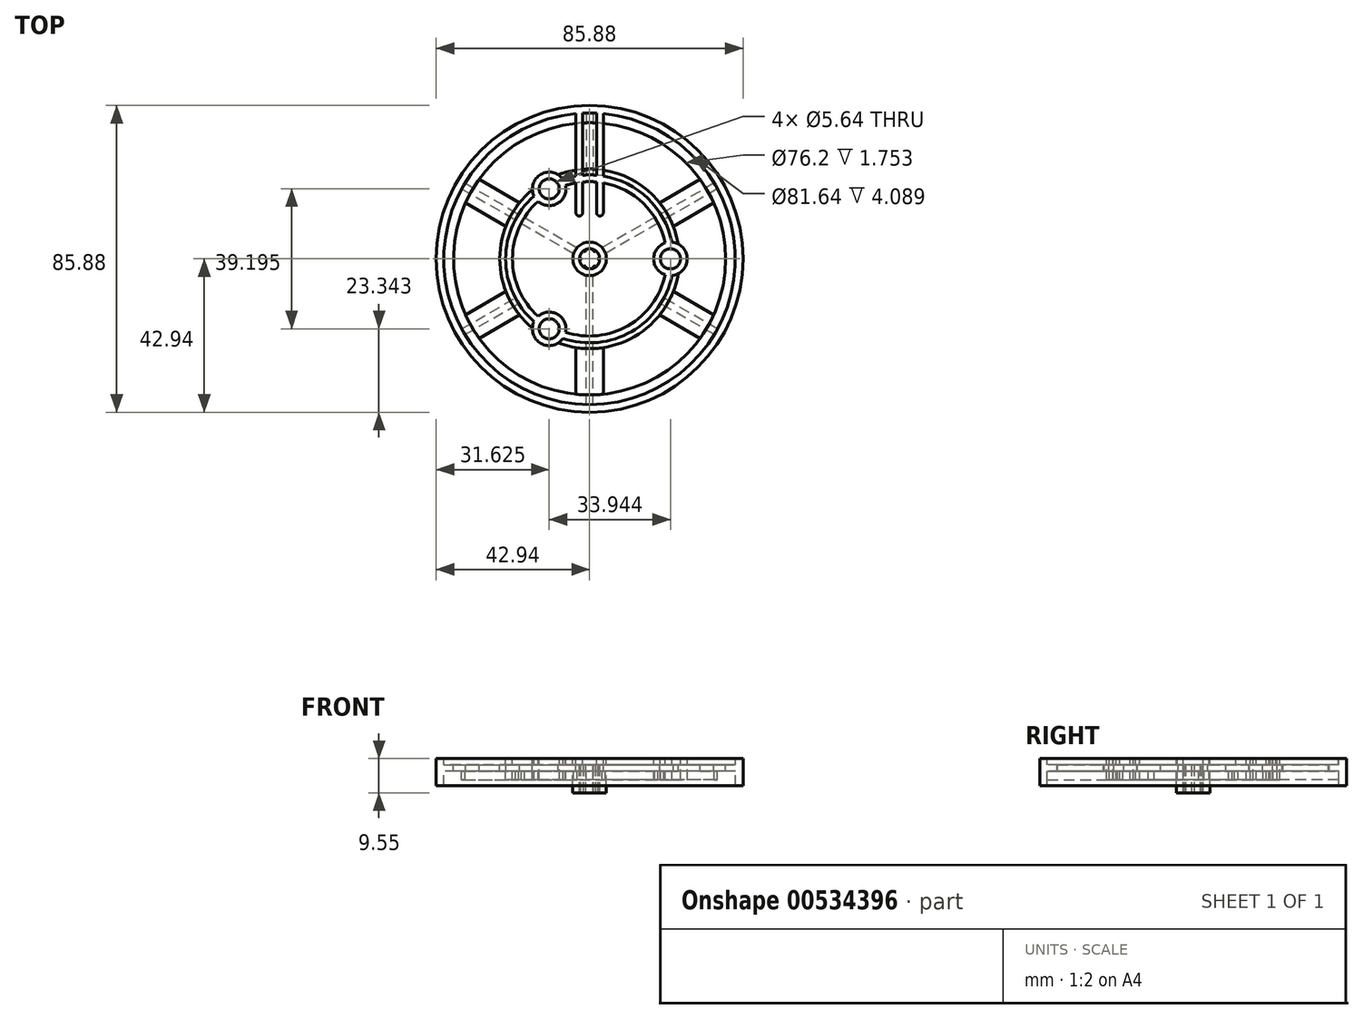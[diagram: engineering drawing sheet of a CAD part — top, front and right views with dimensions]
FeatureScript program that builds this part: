
annotation { "Feature Type Name" : "Feature", "Feature Type Description" : "" }
export const myFeature = defineFeature(function(context is Context, id is Id, definition is map)
    precondition{}
    {
        {
            var Q0;
            Q0=qCreatedBy(makeId("Front.planeOp"),FACE);
            var sketch = newSketch(context, id + "F0", { "sketchPlane" : qUnion([Q0])});
            skLineSegment(sketch, "E0", {"start": v(2.82, 0) * mm, "end": v(2.82, -9.55) * mm});
            skLineSegment(sketch, "E1", {"start": v(2.82, 0) * mm, "end": v(4.7, 0) * mm});
            skLineSegment(sketch, "E2", {"start": v(4.7, 0) * mm, "end": v(4.7, -1.75) * mm});
            skLineSegment(sketch, "E3", {"start": v(4.7, -1.75) * mm, "end": v(21.6, -1.75) * mm});
            skLineSegment(sketch, "E4", {"start": v(21.6, -1.75) * mm, "end": v(21.6, 0) * mm});
            skLineSegment(sketch, "E5", {"start": v(21.6, 0) * mm, "end": v(23.5, 0) * mm});
            skLineSegment(sketch, "E6", {"start": v(23.5, 0) * mm, "end": v(23.5, -1.75) * mm});
            skLineSegment(sketch, "E7", {"start": v(23.5, -1.75) * mm, "end": v(25.15, -1.75) * mm});
            skLineSegment(sketch, "E8", {"start": v(25.15, -1.75) * mm, "end": v(25.15, -3.5) * mm});
            skLineSegment(sketch, "E9", {"start": v(25.15, -3.5) * mm, "end": v(23.5, -3.5) * mm});
            skLineSegment(sketch, "E10", {"start": v(23.5, -3.5) * mm, "end": v(23.5, -5.94) * mm});
            skLineSegment(sketch, "E11", {"start": v(23.5, -5.94) * mm, "end": v(21.6, -5.94) * mm});
            skLineSegment(sketch, "E12", {"start": v(21.6, -5.94) * mm, "end": v(21.6, -3.5) * mm});
            skLineSegment(sketch, "E13", {"start": v(21.6, -3.5) * mm, "end": v(4.7, -3.5) * mm});
            skLineSegment(sketch, "E14", {"start": v(4.7, -3.5) * mm, "end": v(4.7, -9.55) * mm});
            skLineSegment(sketch, "E15", {"start": v(4.7, -9.55) * mm, "end": v(2.82, -9.55) * mm});
            skLineSegment(sketch, "E16", {"start": v(38.1, -1.75) * mm, "end": v(38.1, -3.5) * mm});
            skLineSegment(sketch, "E17", {"start": v(38.1, -3.5) * mm, "end": v(40.82, -3.5) * mm});
            skLineSegment(sketch, "E18", {"start": v(40.82, -3.5) * mm, "end": v(40.82, -7.6) * mm});
            skLineSegment(sketch, "E19", {"start": v(40.82, -7.6) * mm, "end": v(42.94, -7.6) * mm});
            skLineSegment(sketch, "E20", {"start": v(42.94, -7.6) * mm, "end": v(42.94, 0) * mm});
            skLineSegment(sketch, "E21", {"start": v(42.94, 0) * mm, "end": v(40.82, 0) * mm});
            skLineSegment(sketch, "E22", {"start": v(40.82, 0) * mm, "end": v(40.82, -1.75) * mm});
            skLineSegment(sketch, "E23", {"start": v(40.82, -1.75) * mm, "end": v(38.1, -1.75) * mm});
            skLineSegment(sketch, "E24", {"start": v(0, 0) * mm, "end": v(0, -9.55) * mm});
            skSolve(sketch);
        }
        {
            var Q0;
            Q0=qSketchRegion(id+"F0",true);
            var Q1;
            Q1=sQuery(id+"F0.wireOp",EDGE,"E24");
            revolve(context, id + "F1", {"entities" : qUnion([Q0]), "axis" : qUnion([Q1]), "revolveType" : RevolveType.FULL});
        }
        {
            var Q0;
            Q0=makeQuery(id+"F1.opRevolve","SWEPT_FACE",FACE,{"disambiguationData":[OSD([sQuery(id+"F0.wireOp",EDGE,"E21")])]});
            var sketch = newSketch(context, id + "F2", { "sketchPlane" : qUnion([Q0])});
            skCircle(sketch, "E25", {"center": v(0, 0) * mm, "radius": 13.46 * mm, "construction": true});
            skLineSegment(sketch, "E26", {"start": v(-3.82, 40.64) * mm, "end": v(-3.82, 12.9) * mm});
            skLineSegment(sketch, "E27", {"start": v(3.82, 40.64) * mm, "end": v(3.82, 12.9) * mm});
            skLineSegment(sketch, "E28", {"start": v(-1.97, 40.77) * mm, "end": v(-1.97, 12.9) * mm});
            skLineSegment(sketch, "E29", {"start": v(1.97, 40.77) * mm, "end": v(1.97, 12.9) * mm});
            skArc(sketch, "E30", {"start": v(-3.82, 12.9) * mm, "mid": v(-2.9, 11.98) * mm, "end": v(-1.97, 12.9) * mm});
            skArc(sketch, "E31", {"start": v(1.97, 12.9) * mm, "mid": v(2.9, 11.98) * mm, "end": v(3.82, 12.9) * mm});
            skArc(sketch, "E32", {"start": v(-1.97, 40.77) * mm, "mid": v(-2.9, 40.71) * mm, "end": v(-3.82, 40.64) * mm});
            skArc(sketch, "E33", {"start": v(1.97, 40.77) * mm, "mid": v(2.9, 40.71) * mm, "end": v(3.82, 40.64) * mm});
            skSolve(sketch);
        }
        {
            var Q0;
            Q0=makeQuery(id+"F2.imprint","IMPRINT",FACE,{"disambiguationData":[TD([[makeQuery(id+"F2.imprint","IMPRINT",EDGE,{"derivedFrom":sQuery(id+"F2.wireOp",EDGE,"E26")}),1.0]])]});
            var Q1;
            Q1=qSketchRegion(id+"F2",true);
            var Q2;
            Q2=makeQuery(id+"F1.opRevolve","SWEPT_FACE",FACE,{"disambiguationData":[OSD([sQuery(id+"F0.wireOp",EDGE,"E23")])]});
            extrude(context, id + "F3", {"entities" : qUnion([Q0, Q1]), "operationType" : NewBodyOperationType.ADD, "endBound" : BoundingType.UP_TO_SURFACE, "oppositeDirection" : true, "depth" : 25.4 * mm, "endBoundEntityFace" : qUnion([Q2]), "offsetDistance" : 25.4 * mm});
        }
        {
            var Q0;
            Q0=makeQuery(id+"F3.opExtrude","CAP_FACE",FACE,{"disambiguationData":[OSD([sQuery(id+"F2.wireOp",EDGE,"E27"),sQuery(id+"F2.wireOp",EDGE,"E29"),sQuery(id+"F2.wireOp",EDGE,"E31"),sQuery(id+"F2.wireOp",EDGE,"E33")])],"isStart":false});
            var sketch = newSketch(context, id + "F4", { "sketchPlane" : qUnion([Q0])});
            skArc(sketch, "E34.0", {"start": v(-3.82, -24.85) * mm, "mid": v(0, -25.15) * mm, "end": v(3.82, -24.85) * mm});
            skArc(sketch, "E35.0", {"start": v(-3.82, -37.9) * mm, "mid": v(0, -38.1) * mm, "end": v(3.82, -37.9) * mm});
            skLineSegment(sketch, "E36.0", {"start": v(-3.82, -37.9) * mm, "end": v(-3.82, -24.85) * mm});
            skLineSegment(sketch, "E37.0", {"start": v(3.82, -37.9) * mm, "end": v(3.82, -24.85) * mm});
            skPoint(sketch, "E38.orphan", {"position": v(-3.82, -12.9) * mm});
            skPoint(sketch, "E39.orphan", {"position": v(-3.82, -21.26) * mm});
            skSolve(sketch);
        }
        {
            var Q0;
            Q0=qSketchRegion(id+"F4",true);
            var Q1;
            Q1=makeQuery(id+"F1.opRevolve","SWEPT_FACE",FACE,{"disambiguationData":[OSD([sQuery(id+"F0.wireOp",EDGE,"E9")])]});
            extrude(context, id + "F5", {"entities" : qUnion([Q0]), "endBound" : BoundingType.UP_TO_SURFACE, "depth" : 25.4 * mm, "endBoundEntityFace" : qUnion([Q1]), "offsetDistance" : 25.4 * mm});
        }
        {
            var Q0;
            Q0=makeQuery(id+"F5.opExtrude","CAP_FACE",FACE,{"disambiguationData":[OSD([sQuery(id+"F4.wireOp",EDGE,"E34.0"),sQuery(id+"F4.wireOp",EDGE,"E35.0"),sQuery(id+"F4.wireOp",EDGE,"E36.0"),sQuery(id+"F4.wireOp",EDGE,"E37.0")])],"isStart":false});
            var sketch = newSketch(context, id + "F6", { "sketchPlane" : qUnion([Q0])});
            skLineSegment(sketch, "E40", {"start": v(-0.93, -25.13) * mm, "end": v(-0.93, -38.09) * mm});
            skLineSegment(sketch, "E41", {"start": v(0.93, -25.13) * mm, "end": v(0.93, -38.09) * mm});
            skArc(sketch, "E42.0", {"start": v(-0.93, -23.49) * mm, "mid": v(0, -23.5) * mm, "end": v(0.93, -23.49) * mm});
            skArc(sketch, "E43.0", {"start": v(-0.93, -40.8) * mm, "mid": v(0, -40.82) * mm, "end": v(0.93, -40.8) * mm});
            skLineSegment(sketch, "E44", {"start": v(-0.93, -25.13) * mm, "end": v(-0.93, -23.49) * mm});
            skLineSegment(sketch, "E45", {"start": v(0.93, -25.13) * mm, "end": v(0.93, -23.49) * mm});
            skLineSegment(sketch, "E46", {"start": v(-0.93, -38.09) * mm, "end": v(-0.93, -40.8) * mm});
            skLineSegment(sketch, "E47", {"start": v(0.93, -38.09) * mm, "end": v(0.93, -40.8) * mm});
            skLineSegment(sketch, "E48", {"start": v(0, -27.2) * mm, "end": v(0, -23.5) * mm, "construction": true});
            skSolve(sketch);
        }
        {
            var Q0;
            Q0=qSketchRegion(id+"F6",true);
            var Q1;
            Q1=makeQuery(id+"F1.opRevolve","SWEPT_FACE",FACE,{"disambiguationData":[OSD([sQuery(id+"F0.wireOp",EDGE,"E11")])]});
            extrude(context, id + "F7", {"entities" : qUnion([Q0]), "endBound" : BoundingType.UP_TO_SURFACE, "depth" : 25.4 * mm, "endBoundEntityFace" : qUnion([Q1]), "offsetDistance" : 25.4 * mm});
        }
        {
            var Q0;
            Q0=makeQuery(id+"F3.opExtrude","SWEPT_BODY",BODY,{"disambiguationData":[OSD([sQuery(id+"F2.wireOp",EDGE,"E26"),sQuery(id+"F2.wireOp",EDGE,"E28"),sQuery(id+"F2.wireOp",EDGE,"E30"),sQuery(id+"F2.wireOp",EDGE,"E32")])]});
            var Q1;
            Q1=makeQuery(id+"F3.opExtrude","SWEPT_BODY",BODY,{"disambiguationData":[OSD([sQuery(id+"F2.wireOp",EDGE,"E27"),sQuery(id+"F2.wireOp",EDGE,"E29"),sQuery(id+"F2.wireOp",EDGE,"E31"),sQuery(id+"F2.wireOp",EDGE,"E33")])]});
            var Q2;
            Q2=makeQuery(id+"F5.opExtrude","SWEPT_BODY",BODY,{"disambiguationData":[OSD([sQuery(id+"F4.wireOp",EDGE,"E34.0"),sQuery(id+"F4.wireOp",EDGE,"E35.0"),sQuery(id+"F4.wireOp",EDGE,"E36.0"),sQuery(id+"F4.wireOp",EDGE,"E37.0")])]});
            var Q3;
            Q3=makeQuery(id+"F7.opExtrude","SWEPT_BODY",BODY,{"disambiguationData":[OSD([sQuery(id+"F6.wireOp",EDGE,"E40"),sQuery(id+"F6.wireOp",EDGE,"E41"),sQuery(id+"F6.wireOp",EDGE,"E42.0"),sQuery(id+"F6.wireOp",EDGE,"E43.0"),sQuery(id+"F6.wireOp",EDGE,"E44"),sQuery(id+"F6.wireOp",EDGE,"E45"),sQuery(id+"F6.wireOp",EDGE,"E46"),sQuery(id+"F6.wireOp",EDGE,"E47")])]});
            var Q4;
            Q4=makeQuery(id+"F1.opRevolve","SWEPT_EDGE",EDGE,{"disambiguationData":[OSD([sQuery(id+"F0.wireOp",EDGE,"E0"),sQuery(id+"F0.wireOp",EDGE,"E15")])]});
            circularPattern(context, id + "F8", {"entities" : qUnion([Q0, Q1, Q2, Q3]), "axis" : qUnion([Q4]), "angle" : 360 * degree, "instanceCount" : 6, "equalSpace" : true});
        }
        {
            var Q0;
            Q0=makeQuery(id+"F1.opRevolve","SWEPT_FACE",FACE,{"disambiguationData":[OSD([sQuery(id+"F0.wireOp",EDGE,"E13")])]});
            var sketch = newSketch(context, id + "F9", { "sketchPlane" : qUnion([Q0])});
            skArc(sketch, "E49.0", {"start": v(0.93, 21.58) * mm, "mid": v(0, 21.6) * mm, "end": v(-0.93, 21.58) * mm});
            skArc(sketch, "E50.0", {"start": v(0.93, 4.6) * mm, "mid": v(0, 4.7) * mm, "end": v(-0.93, 4.6) * mm});
            skLineSegment(sketch, "E51", {"start": v(-0.93, 21.58) * mm, "end": v(-0.93, 4.6) * mm});
            skLineSegment(sketch, "E52", {"start": v(0.93, 21.58) * mm, "end": v(0.93, 4.6) * mm});
            skPoint(sketch, "E53.0.end.orphan", {"position": v(-0.93, 23.49) * mm});
            skPoint(sketch, "E53.0.start.orphan", {"position": v(-0.93, 40.8) * mm});
            skArc(sketch, "E54", {"start": v(-0.93, 21.58) * mm, "mid": v(0, 21.6) * mm, "end": v(0.93, 21.58) * mm});
            skArc(sketch, "E55", {"start": v(-0.93, 4.6) * mm, "mid": v(0, 4.7) * mm, "end": v(0.93, 4.6) * mm});
            skSolve(sketch);
        }
        {
            var Q0;
            Q0=makeQuery(id+"F9.imprint","IMPRINT",FACE,{"disambiguationData":[TD([[makeQuery(id+"F9.imprint","IMPRINT",EDGE,{"derivedFrom":sQuery(id+"F9.wireOp",EDGE,"E51")}),1.0]])]});
            var Q1;
            Q1=makeQuery(id+"F1.opRevolve","SWEPT_FACE",FACE,{"disambiguationData":[OSD([sQuery(id+"F0.wireOp",EDGE,"E11")])]});
            extrude(context, id + "F10", {"entities" : qUnion([Q0]), "endBound" : BoundingType.UP_TO_SURFACE, "depth" : 25.4 * mm, "endBoundEntityFace" : qUnion([Q1]), "offsetDistance" : 25.4 * mm});
        }
        {
            var Q0;
            Q0=makeQuery(id+"F10.opExtrude","SWEPT_BODY",BODY,{"disambiguationData":[OSD([sQuery(id+"F9.wireOp",EDGE,"E51"),sQuery(id+"F9.wireOp",EDGE,"E52"),sQuery(id+"F9.wireOp",EDGE,"E54"),sQuery(id+"F9.wireOp",EDGE,"E55")])]});
            var Q1;
            Q1=makeQuery(id+"F1.opRevolve","SWEPT_EDGE",EDGE,{"disambiguationData":[OSD([sQuery(id+"F0.wireOp",EDGE,"E0"),sQuery(id+"F0.wireOp",EDGE,"E1")])]});
            circularPattern(context, id + "F11", {"entities" : qUnion([Q0]), "axis" : qUnion([Q1]), "angle" : 360 * degree, "instanceCount" : 3, "equalSpace" : true});
        }
        {
            var Q0;
            Q0=makeQuery(id+"F1.opRevolve","SWEPT_FACE",FACE,{"disambiguationData":[OSD([sQuery(id+"F0.wireOp",EDGE,"E5")])]});
            var sketch = newSketch(context, id + "F12", { "sketchPlane" : qUnion([Q0])});
            skCircle(sketch, "E56", {"center": v(-11.31, -19.6) * mm, "radius": 4.69 * mm});
            skLineSegment(sketch, "E57", {"start": v(0, 0) * mm, "end": v(-11.31, -19.6) * mm, "construction": true});
            skLineSegment(sketch, "E58", {"start": v(0, 0) * mm, "end": v(-11.31, 19.6) * mm, "construction": true});
            skLineSegment(sketch, "E59", {"start": v(0, 0) * mm, "end": v(22.63, 0) * mm, "construction": true});
            skCircle(sketch, "E60", {"center": v(-11.31, 19.6) * mm, "radius": 4.69 * mm});
            skCircle(sketch, "E61", {"center": v(22.63, 0) * mm, "radius": 4.69 * mm});
            skSolve(sketch);
        }
        {
            var Q0;
            {var subQ0=sQuery(id+"F12.wireOp",EDGE,"E56");var subQ1=makeQuery(id+"F1.opRevolve","SWEPT_EDGE",EDGE,{"disambiguationData":[OSD([sQuery(id+"F0.wireOp",EDGE,"E5"),sQuery(id+"F0.wireOp",EDGE,"E6")])]});var subQ2=makeQuery(id+"F12.imprint","INTERSECT",VERTEX,{"disambiguationData":[OD(0.0)],"derivedFrom":[subQ1,subQ0]});Q0=makeQuery(id+"F12.imprint","IMPRINT",FACE,{"disambiguationData":[TD([[makeQuery(id+"F12.imprint","IMPRINT",EDGE,{"disambiguationData":[TD([[subQ2,-1.0]])],"derivedFrom":subQ0}),1.0]])]});}
            var Q1;
            {var subQ0=sQuery(id+"F12.wireOp",EDGE,"E56");var subQ1=makeQuery(id+"F1.opRevolve","SWEPT_EDGE",EDGE,{"disambiguationData":[OSD([sQuery(id+"F0.wireOp",EDGE,"E4"),sQuery(id+"F0.wireOp",EDGE,"E5")])]});var subQ2=makeQuery(id+"F12.imprint","INTERSECT",VERTEX,{"disambiguationData":[OD(0.0)],"derivedFrom":[subQ1,subQ0]});Q1=makeQuery(id+"F12.imprint","IMPRINT",FACE,{"disambiguationData":[TD([[makeQuery(id+"F12.imprint","IMPRINT",EDGE,{"disambiguationData":[TD([[subQ2,1.0]])],"derivedFrom":subQ0}),1.0]])]});}
            var Q2;
            {var subQ0=sQuery(id+"F12.wireOp",EDGE,"E60");var subQ1=makeQuery(id+"F1.opRevolve","SWEPT_EDGE",EDGE,{"disambiguationData":[OSD([sQuery(id+"F0.wireOp",EDGE,"E5"),sQuery(id+"F0.wireOp",EDGE,"E6")])]});var subQ2=makeQuery(id+"F12.imprint","INTERSECT",VERTEX,{"disambiguationData":[OD(0.0)],"derivedFrom":[subQ1,subQ0]});Q2=makeQuery(id+"F12.imprint","IMPRINT",FACE,{"disambiguationData":[TD([[makeQuery(id+"F12.imprint","IMPRINT",EDGE,{"disambiguationData":[TD([[subQ2,-1.0]])],"derivedFrom":subQ0}),1.0]])]});}
            var Q3;
            {var subQ0=sQuery(id+"F12.wireOp",EDGE,"E60");var subQ1=makeQuery(id+"F1.opRevolve","SWEPT_EDGE",EDGE,{"disambiguationData":[OSD([sQuery(id+"F0.wireOp",EDGE,"E4"),sQuery(id+"F0.wireOp",EDGE,"E5")])]});var subQ2=makeQuery(id+"F12.imprint","INTERSECT",VERTEX,{"disambiguationData":[OD(0.0)],"derivedFrom":[subQ1,subQ0]});Q3=makeQuery(id+"F12.imprint","IMPRINT",FACE,{"disambiguationData":[TD([[makeQuery(id+"F12.imprint","IMPRINT",EDGE,{"disambiguationData":[TD([[subQ2,1.0]])],"derivedFrom":subQ0}),1.0]])]});}
            var Q4;
            {var subQ0=sQuery(id+"F12.wireOp",EDGE,"E61");var subQ1=makeQuery(id+"F1.opRevolve","SWEPT_EDGE",EDGE,{"disambiguationData":[OSD([sQuery(id+"F0.wireOp",EDGE,"E5"),sQuery(id+"F0.wireOp",EDGE,"E6")])]});var subQ2=makeQuery(id+"F12.imprint","INTERSECT",VERTEX,{"disambiguationData":[OD(0.0)],"derivedFrom":[subQ1,subQ0]});Q4=makeQuery(id+"F12.imprint","IMPRINT",FACE,{"disambiguationData":[TD([[makeQuery(id+"F12.imprint","IMPRINT",EDGE,{"disambiguationData":[TD([[subQ2,1.0]])],"derivedFrom":subQ0}),1.0]])]});}
            var Q5;
            {var subQ0=sQuery(id+"F12.wireOp",EDGE,"E61");var subQ1=makeQuery(id+"F1.opRevolve","SWEPT_EDGE",EDGE,{"disambiguationData":[OSD([sQuery(id+"F0.wireOp",EDGE,"E4"),sQuery(id+"F0.wireOp",EDGE,"E5")])]});var subQ2=makeQuery(id+"F12.imprint","INTERSECT",VERTEX,{"disambiguationData":[OD(0.0)],"derivedFrom":[subQ1,subQ0]});Q5=makeQuery(id+"F12.imprint","IMPRINT",FACE,{"disambiguationData":[TD([[makeQuery(id+"F12.imprint","IMPRINT",EDGE,{"disambiguationData":[TD([[subQ2,-1.0]])],"derivedFrom":subQ0}),1.0]])]});}
            var Q6;
            Q6=sQuery(id+"F12.wireOp",EDGE,"E56");
            var Q7;
            Q7=makeQuery(id+"F1.opRevolve","SWEPT_FACE",FACE,{"disambiguationData":[OSD([sQuery(id+"F0.wireOp",EDGE,"E11")])]});
            extrude(context, id + "F13", {"entities" : qUnion([Q0, Q1, Q2, Q3, Q4, Q5]), "operationType" : NewBodyOperationType.ADD, "surfaceEntities" : qUnion([Q6]), "endBound" : BoundingType.UP_TO_SURFACE, "oppositeDirection" : true, "depth" : 25.4 * mm, "endBoundEntityFace" : qUnion([Q7]), "offsetDistance" : 25.4 * mm});
        }
        {
            var Q0;
            {var subQ0=sQuery(id+"F12.wireOp",EDGE,"E61");var subQ1=sQuery(id+"F0.wireOp",EDGE,"E6");var subQ2=sQuery(id+"F0.wireOp",EDGE,"E5");var subQ3=sQuery(id+"F0.wireOp",EDGE,"E4");var subQ4=sQuery(id+"F12.wireOp",EDGE,"E60");var subQ5=sQuery(id+"F12.wireOp",EDGE,"E56");Q0=makeQuery(id+"F13.boolean.opBoolean","MERGE",FACE,{"derivedFrom":[makeQuery(id+"F3.boolean.opBoolean","MERGE",FACE,{"derivedFrom":[makeQuery(id+"F1.opRevolve","SWEPT_FACE",FACE,{"disambiguationData":[OSD([subQ2])]}),makeQuery(id+"F1.opRevolve","SWEPT_FACE",FACE,{"disambiguationData":[OSD([sQuery(id+"F0.wireOp",EDGE,"E21")])]}),makeQuery(id+"F3.opExtrude","CAP_FACE",FACE,{"disambiguationData":[OSD([sQuery(id+"F2.wireOp",EDGE,"E26"),sQuery(id+"F2.wireOp",EDGE,"E28"),sQuery(id+"F2.wireOp",EDGE,"E30"),sQuery(id+"F2.wireOp",EDGE,"E32")])],"isStart":true}),makeQuery(id+"F3.opExtrude","CAP_FACE",FACE,{"disambiguationData":[OSD([sQuery(id+"F2.wireOp",EDGE,"E27"),sQuery(id+"F2.wireOp",EDGE,"E29"),sQuery(id+"F2.wireOp",EDGE,"E31"),sQuery(id+"F2.wireOp",EDGE,"E33")])],"isStart":true})]}),makeQuery(id+"F13.opExtrude","CAP_FACE",FACE,{"disambiguationData":[OSD([subQ2,subQ1,subQ5])],"isStart":true}),makeQuery(id+"F13.opExtrude","CAP_FACE",FACE,{"disambiguationData":[OSD([subQ3,subQ2,subQ5])],"isStart":true}),makeQuery(id+"F13.opExtrude","CAP_FACE",FACE,{"disambiguationData":[OSD([subQ2,subQ1,subQ4])],"isStart":true}),makeQuery(id+"F13.opExtrude","CAP_FACE",FACE,{"disambiguationData":[OSD([subQ3,subQ2,subQ4])],"isStart":true}),makeQuery(id+"F13.opExtrude","CAP_FACE",FACE,{"disambiguationData":[OSD([subQ3,subQ2,subQ0])],"isStart":true}),makeQuery(id+"F13.opExtrude","CAP_FACE",FACE,{"disambiguationData":[OSD([subQ2,subQ1,subQ0])],"isStart":true})]});}
            var sketch = newSketch(context, id + "F14", { "sketchPlane" : qUnion([Q0])});
            skArc(sketch, "E62.0", {"start": v(-15.56, -17.62) * mm, "mid": v(-13.66, -23.66) * mm, "end": v(-7.48, -22.29) * mm, "construction": true});
            skSolve(sketch);
        }
        {
            var Q0;
            Q0=sQuery(id+"F14.wireOp",VERTEX,"E62.0.center");
            var Q1;
            Q1=makeQuery(id+"F1.opRevolve","SWEPT_BODY",BODY,{"disambiguationData":[OSD([sQuery(id+"F0.wireOp",EDGE,"E0"),sQuery(id+"F0.wireOp",EDGE,"E1"),sQuery(id+"F0.wireOp",EDGE,"E2"),sQuery(id+"F0.wireOp",EDGE,"E3"),sQuery(id+"F0.wireOp",EDGE,"E4"),sQuery(id+"F0.wireOp",EDGE,"E5"),sQuery(id+"F0.wireOp",EDGE,"E6"),sQuery(id+"F0.wireOp",EDGE,"E7"),sQuery(id+"F0.wireOp",EDGE,"E8"),sQuery(id+"F0.wireOp",EDGE,"E9"),sQuery(id+"F0.wireOp",EDGE,"E10"),sQuery(id+"F0.wireOp",EDGE,"E11"),sQuery(id+"F0.wireOp",EDGE,"E12"),sQuery(id+"F0.wireOp",EDGE,"E13"),sQuery(id+"F0.wireOp",EDGE,"E14"),sQuery(id+"F0.wireOp",EDGE,"E15")])]});
            hole(context, id + "F15", {"style" : HoleStyle.SIMPLE, "endStyle" : HoleEndStyle.THROUGH, "holeDiameter" : 5.64 * mm, "isTappedThrough" : true, "tappedDepth" : 12.7 * mm, "tapClearance" : 3, "locations" : qUnion([Q0]), "scope" : qUnion([Q1])});
        }
        {
            var Q0;
            Q0=makeQuery(id+"F1.opRevolve","SWEPT_FACE",FACE,{"disambiguationData":[OSD([sQuery(id+"F0.wireOp",EDGE,"E1")])]});
            var sketch = newSketch(context, id + "F16", { "sketchPlane" : qUnion([Q0])});
            skLineSegment(sketch, "E63", {"start": v(-1.4, -2.42) * mm, "end": v(-1.4, -2.44) * mm, "construction": true});
            skArc(sketch, "E64", {"start": v(-1.07, -2.6) * mm, "mid": v(-1.2, -2.09) * mm, "end": v(-1.73, -2.23) * mm});
            skArc(sketch, "E65", {"start": v(-1.73, -2.23) * mm, "mid": v(-1.4, -2.44) * mm, "end": v(-1.07, -2.6) * mm});
            skSolve(sketch);
        }
        {
            var Q0;
            Q0=makeQuery(id+"F16.imprint","IMPRINT",FACE,{"disambiguationData":[TD([[makeQuery(id+"F16.imprint","IMPRINT",EDGE,{"derivedFrom":sQuery(id+"F16.wireOp",EDGE,"E64")}),1.0]])]});
            var Q1;
            Q1=sQuery(id+"F16.wireOp",EDGE,"E64");
            var Q2;
            Q2=makeQuery(id+"F1.opRevolve","SWEPT_FACE",FACE,{"disambiguationData":[OSD([sQuery(id+"F0.wireOp",EDGE,"E15")])]});
            extrude(context, id + "F17", {"entities" : qUnion([Q0]), "surfaceEntities" : qUnion([Q1]), "endBound" : BoundingType.UP_TO_SURFACE, "oppositeDirection" : true, "depth" : 25.4 * mm, "endBoundEntityFace" : qUnion([Q2]), "offsetDistance" : 25.4 * mm});
        }
        {
            var Q0;
            Q0=makeQuery(id+"F17.opExtrude","SWEPT_BODY",BODY,{"disambiguationData":[OSD([sQuery(id+"F16.wireOp",EDGE,"E64"),sQuery(id+"F16.wireOp",EDGE,"E65")])]});
            var Q1;
            Q1=makeQuery(id+"F1.opRevolve","SWEPT_FACE",FACE,{"disambiguationData":[OSD([sQuery(id+"F0.wireOp",EDGE,"E0")])]});
            circularPattern(context, id + "F18", {"entities" : qUnion([Q0]), "axis" : qUnion([Q1]), "angle" : 360 * degree, "instanceCount" : 6, "equalSpace" : true});
        }
        {
            var Q0;
            {var subQ0=sQuery(id+"F12.wireOp",EDGE,"E61");var subQ1=sQuery(id+"F0.wireOp",EDGE,"E6");var subQ2=sQuery(id+"F0.wireOp",EDGE,"E5");var subQ3=sQuery(id+"F0.wireOp",EDGE,"E4");var subQ4=sQuery(id+"F12.wireOp",EDGE,"E60");var subQ5=sQuery(id+"F12.wireOp",EDGE,"E56");Q0=makeQuery(id+"F13.boolean.opBoolean","MERGE",FACE,{"derivedFrom":[makeQuery(id+"F3.boolean.opBoolean","MERGE",FACE,{"derivedFrom":[makeQuery(id+"F1.opRevolve","SWEPT_FACE",FACE,{"disambiguationData":[OSD([subQ2])]}),makeQuery(id+"F1.opRevolve","SWEPT_FACE",FACE,{"disambiguationData":[OSD([sQuery(id+"F0.wireOp",EDGE,"E21")])]}),makeQuery(id+"F3.opExtrude","CAP_FACE",FACE,{"disambiguationData":[OSD([sQuery(id+"F2.wireOp",EDGE,"E26"),sQuery(id+"F2.wireOp",EDGE,"E28"),sQuery(id+"F2.wireOp",EDGE,"E30"),sQuery(id+"F2.wireOp",EDGE,"E32")])],"isStart":true}),makeQuery(id+"F3.opExtrude","CAP_FACE",FACE,{"disambiguationData":[OSD([sQuery(id+"F2.wireOp",EDGE,"E27"),sQuery(id+"F2.wireOp",EDGE,"E29"),sQuery(id+"F2.wireOp",EDGE,"E31"),sQuery(id+"F2.wireOp",EDGE,"E33")])],"isStart":true})]}),makeQuery(id+"F13.opExtrude","CAP_FACE",FACE,{"disambiguationData":[OSD([subQ2,subQ1,subQ5])],"isStart":true}),makeQuery(id+"F13.opExtrude","CAP_FACE",FACE,{"disambiguationData":[OSD([subQ3,subQ2,subQ5])],"isStart":true}),makeQuery(id+"F13.opExtrude","CAP_FACE",FACE,{"disambiguationData":[OSD([subQ2,subQ1,subQ4])],"isStart":true}),makeQuery(id+"F13.opExtrude","CAP_FACE",FACE,{"disambiguationData":[OSD([subQ3,subQ2,subQ4])],"isStart":true}),makeQuery(id+"F13.opExtrude","CAP_FACE",FACE,{"disambiguationData":[OSD([subQ3,subQ2,subQ0])],"isStart":true}),makeQuery(id+"F13.opExtrude","CAP_FACE",FACE,{"disambiguationData":[OSD([subQ2,subQ1,subQ0])],"isStart":true})]});}
            var sketch = newSketch(context, id + "F19", { "sketchPlane" : qUnion([Q0])});
            skArc(sketch, "E66.0", {"start": v(-7.48, 22.29) * mm, "mid": v(-13.66, 23.66) * mm, "end": v(-15.56, 17.62) * mm, "construction": true});
            skArc(sketch, "E67.0", {"start": v(23.04, -4.67) * mm, "mid": v(27.32, 0) * mm, "end": v(23.04, 4.67) * mm, "construction": true});
            skSolve(sketch);
        }
        {
            var Q0;
            Q0=sQuery(id+"F19.wireOp",VERTEX,"E66.0.center");
            var Q1;
            Q1=makeQuery(id+"F1.opRevolve","SWEPT_BODY",BODY,{"disambiguationData":[OSD([sQuery(id+"F0.wireOp",EDGE,"E0"),sQuery(id+"F0.wireOp",EDGE,"E1"),sQuery(id+"F0.wireOp",EDGE,"E2"),sQuery(id+"F0.wireOp",EDGE,"E3"),sQuery(id+"F0.wireOp",EDGE,"E4"),sQuery(id+"F0.wireOp",EDGE,"E5"),sQuery(id+"F0.wireOp",EDGE,"E6"),sQuery(id+"F0.wireOp",EDGE,"E7"),sQuery(id+"F0.wireOp",EDGE,"E8"),sQuery(id+"F0.wireOp",EDGE,"E9"),sQuery(id+"F0.wireOp",EDGE,"E10"),sQuery(id+"F0.wireOp",EDGE,"E11"),sQuery(id+"F0.wireOp",EDGE,"E12"),sQuery(id+"F0.wireOp",EDGE,"E13"),sQuery(id+"F0.wireOp",EDGE,"E14"),sQuery(id+"F0.wireOp",EDGE,"E15")])]});
            hole(context, id + "F20", {"style" : HoleStyle.SIMPLE, "endStyle" : HoleEndStyle.THROUGH, "holeDiameter" : 5.64 * mm, "isTappedThrough" : true, "tappedDepth" : 12.7 * mm, "tapClearance" : 3, "locations" : qUnion([Q0]), "scope" : qUnion([Q1])});
        }
        {
            var Q0;
            {var subQ0=sQuery(id+"F12.wireOp",EDGE,"E61");var subQ1=sQuery(id+"F0.wireOp",EDGE,"E6");var subQ2=sQuery(id+"F0.wireOp",EDGE,"E5");var subQ3=sQuery(id+"F0.wireOp",EDGE,"E4");var subQ4=sQuery(id+"F12.wireOp",EDGE,"E60");var subQ5=sQuery(id+"F12.wireOp",EDGE,"E56");Q0=makeQuery(id+"F13.boolean.opBoolean","MERGE",FACE,{"derivedFrom":[makeQuery(id+"F3.boolean.opBoolean","MERGE",FACE,{"derivedFrom":[makeQuery(id+"F1.opRevolve","SWEPT_FACE",FACE,{"disambiguationData":[OSD([subQ2])]}),makeQuery(id+"F1.opRevolve","SWEPT_FACE",FACE,{"disambiguationData":[OSD([sQuery(id+"F0.wireOp",EDGE,"E21")])]}),makeQuery(id+"F3.opExtrude","CAP_FACE",FACE,{"disambiguationData":[OSD([sQuery(id+"F2.wireOp",EDGE,"E26"),sQuery(id+"F2.wireOp",EDGE,"E28"),sQuery(id+"F2.wireOp",EDGE,"E30"),sQuery(id+"F2.wireOp",EDGE,"E32")])],"isStart":true}),makeQuery(id+"F3.opExtrude","CAP_FACE",FACE,{"disambiguationData":[OSD([sQuery(id+"F2.wireOp",EDGE,"E27"),sQuery(id+"F2.wireOp",EDGE,"E29"),sQuery(id+"F2.wireOp",EDGE,"E31"),sQuery(id+"F2.wireOp",EDGE,"E33")])],"isStart":true})]}),makeQuery(id+"F13.opExtrude","CAP_FACE",FACE,{"disambiguationData":[OSD([subQ2,subQ1,subQ5])],"isStart":true}),makeQuery(id+"F13.opExtrude","CAP_FACE",FACE,{"disambiguationData":[OSD([subQ3,subQ2,subQ5])],"isStart":true}),makeQuery(id+"F13.opExtrude","CAP_FACE",FACE,{"disambiguationData":[OSD([subQ2,subQ1,subQ4])],"isStart":true}),makeQuery(id+"F13.opExtrude","CAP_FACE",FACE,{"disambiguationData":[OSD([subQ3,subQ2,subQ4])],"isStart":true}),makeQuery(id+"F13.opExtrude","CAP_FACE",FACE,{"disambiguationData":[OSD([subQ3,subQ2,subQ0])],"isStart":true}),makeQuery(id+"F13.opExtrude","CAP_FACE",FACE,{"disambiguationData":[OSD([subQ2,subQ1,subQ0])],"isStart":true})]});}
            var sketch = newSketch(context, id + "F21", { "sketchPlane" : qUnion([Q0])});
            skArc(sketch, "E68.0", {"start": v(23.04, -4.67) * mm, "mid": v(27.32, 0) * mm, "end": v(23.04, 4.67) * mm, "construction": true});
            skSolve(sketch);
        }
        {
            var Q0;
            Q0=sQuery(id+"F21.wireOp",VERTEX,"E68.0.center");
            var Q1;
            Q1=makeQuery(id+"F1.opRevolve","SWEPT_BODY",BODY,{"disambiguationData":[OSD([sQuery(id+"F0.wireOp",EDGE,"E0"),sQuery(id+"F0.wireOp",EDGE,"E1"),sQuery(id+"F0.wireOp",EDGE,"E2"),sQuery(id+"F0.wireOp",EDGE,"E3"),sQuery(id+"F0.wireOp",EDGE,"E4"),sQuery(id+"F0.wireOp",EDGE,"E5"),sQuery(id+"F0.wireOp",EDGE,"E6"),sQuery(id+"F0.wireOp",EDGE,"E7"),sQuery(id+"F0.wireOp",EDGE,"E8"),sQuery(id+"F0.wireOp",EDGE,"E9"),sQuery(id+"F0.wireOp",EDGE,"E10"),sQuery(id+"F0.wireOp",EDGE,"E11"),sQuery(id+"F0.wireOp",EDGE,"E12"),sQuery(id+"F0.wireOp",EDGE,"E13"),sQuery(id+"F0.wireOp",EDGE,"E14"),sQuery(id+"F0.wireOp",EDGE,"E15")])]});
            hole(context, id + "F22", {"style" : HoleStyle.SIMPLE, "endStyle" : HoleEndStyle.THROUGH, "holeDiameter" : 5.64 * mm, "isTappedThrough" : true, "tappedDepth" : 12.7 * mm, "tapClearance" : 3, "locations" : qUnion([Q0]), "scope" : qUnion([Q1])});
        }
    });
